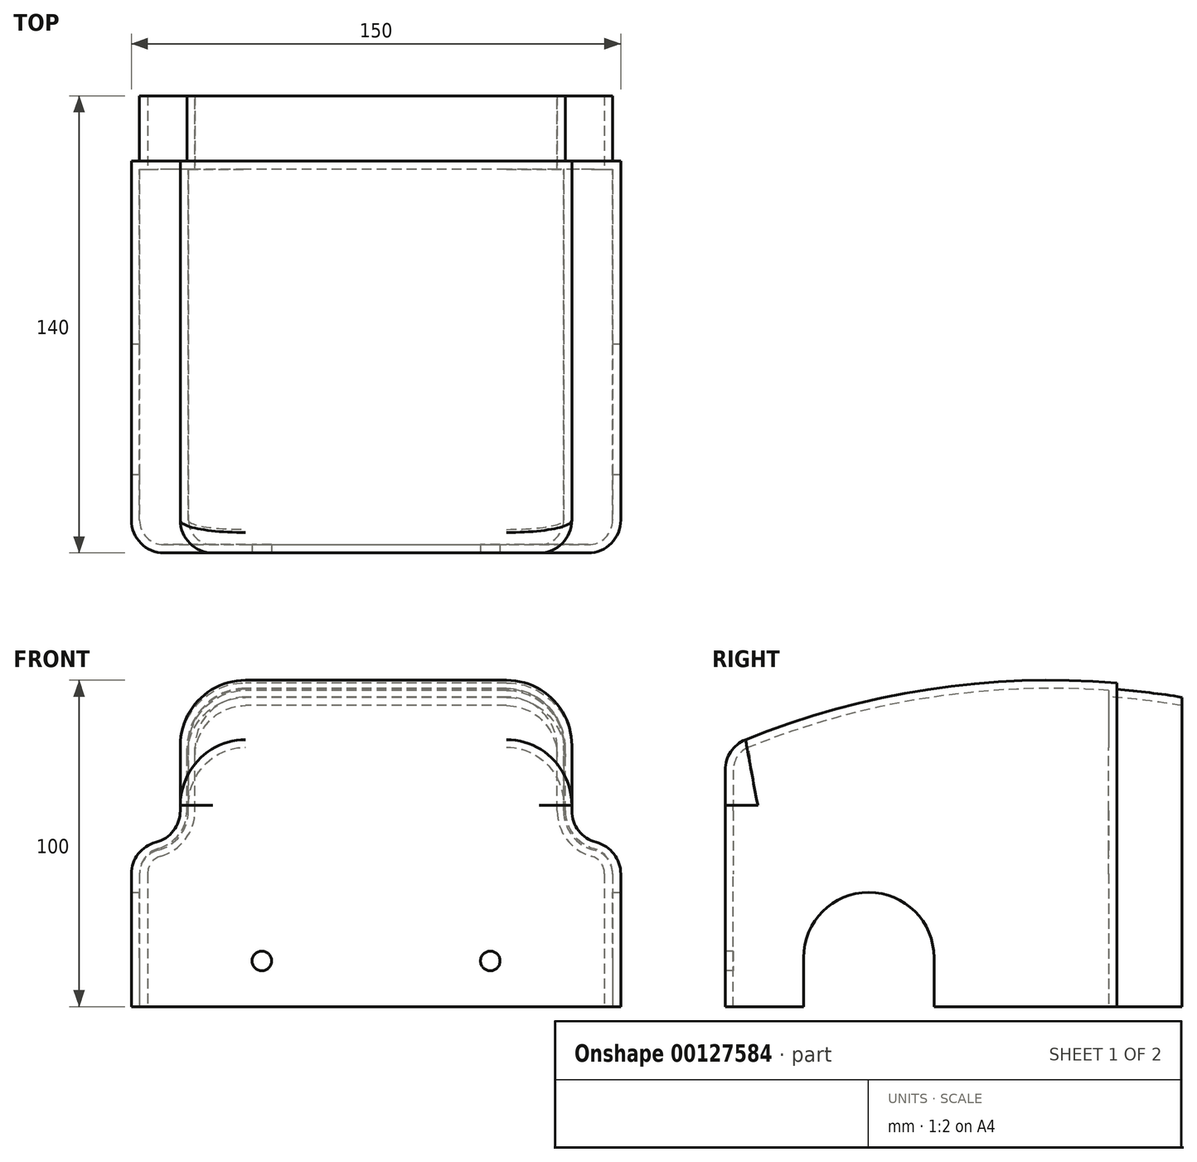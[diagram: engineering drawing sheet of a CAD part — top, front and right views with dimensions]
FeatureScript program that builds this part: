
annotation { "Feature Type Name" : "Feature", "Feature Type Description" : "" }
export const myFeature = defineFeature(function(context is Context, id is Id, definition is map)
    precondition{}
    {
        {
            var Q0;
            Q0=qCreatedBy(makeId("Top.planeOp"),FACE);
            var sketch = newSketch(context, id + "F0", { "sketchPlane" : qUnion([Q0])});
            skLineSegment(sketch, "E0.bottom", {"start": v(-75, 120) * mm, "end": v(75, 120) * mm});
            skLineSegment(sketch, "E0.top", {"start": v(-75, 0) * mm, "end": v(75, 0) * mm});
            skLineSegment(sketch, "E0.left", {"start": v(-75, 120) * mm, "end": v(-75, 0) * mm});
            skLineSegment(sketch, "E0.right", {"start": v(75, 120) * mm, "end": v(75, 0) * mm});
            skSolve(sketch);
        }
        {
            var Q0;
            {var subQ1=sQuery(id+"F0.wireOp",EDGE,"E0.top");Q0=makeQuery(id+"F0.imprint","IMPRINT",FACE,{"disambiguationData":[TD([[makeQuery(id+"F0.imprint","IMPRINT",EDGE,{"derivedFrom":subQ1}),1.0]])]});}
            extrude(context, id + "F1", {"entities" : qUnion([Q0]), "depth" : 50 * mm});
        }
        {
            var Q0;
            Q0=qCreatedBy(makeId("Top.planeOp"),FACE);
            var sketch = newSketch(context, id + "F2", { "sketchPlane" : qUnion([Q0])});
            skLineSegment(sketch, "E1.bottom", {"start": v(72.5, 140) * mm, "end": v(-72.5, 140) * mm});
            skLineSegment(sketch, "E1.top", {"start": v(72.5, 120) * mm, "end": v(-72.5, 120) * mm});
            skLineSegment(sketch, "E1.left", {"start": v(72.5, 140) * mm, "end": v(72.5, 120) * mm});
            skLineSegment(sketch, "E1.right", {"start": v(-72.5, 140) * mm, "end": v(-72.5, 120) * mm});
            skSolve(sketch);
        }
        {
            var Q0;
            Q0=makeQuery(id+"F2.imprint","IMPRINT",FACE,{"disambiguationData":[TD([[makeQuery(id+"F2.imprint","IMPRINT",EDGE,{"derivedFrom":sQuery(id+"F2.wireOp",EDGE,"E1.bottom")}),1.0]])]});
            extrude(context, id + "F3", {"entities" : qUnion([Q0]), "operationType" : NewBodyOperationType.ADD, "depth" : 48 * mm});
        }
        {
            var Q0;
            Q0=qCreatedBy(makeId("Right.planeOp"),FACE);
            var sketch = newSketch(context, id + "F4", { "sketchPlane" : qUnion([Q0])});
            skCircle(sketch, "E2", {"center": v(100, -150) * mm, "radius": 250 * mm});
            skLineSegment(sketch, "E3.bottom", {"start": v(0, 0) * mm, "end": v(120, 0) * mm});
            skLineSegment(sketch, "E3.left", {"start": v(0, 0) * mm, "end": v(0, 79.13) * mm});
            skLineSegment(sketch, "E3.right", {"start": v(120, 0) * mm, "end": v(120, 99.2) * mm});
            skSolve(sketch);
        }
        {
            var Q0;
            {var subQ0=sQuery(id+"F4.wireOp",EDGE,"E3.top");Q0=makeQuery(id+"F4.imprint","IMPRINT",FACE,{"disambiguationData":[TD([[makeQuery(id+"F4.imprint","IMPRINT",EDGE,{"derivedFrom":subQ0}),1.0]])]});}
            var Q1;
            Q1=makeQuery(id+"F4.imprint","IMPRINT",FACE,{"disambiguationData":[TD([[makeQuery(id+"F4.imprint","IMPRINT",EDGE,{"derivedFrom":sQuery(id+"F4.wireOp",EDGE,"E3.bottom")}),1.0]])]});
            extrude(context, id + "F5", {"entities" : qUnion([Q0, Q1]), "operationType" : NewBodyOperationType.ADD, "endBound" : BoundingType.SYMMETRIC, "depth" : 120 * mm});
        }
        {
            var Q0;
            Q0=qCreatedBy(makeId("Right.planeOp"),FACE);
            var sketch = newSketch(context, id + "F6", { "sketchPlane" : qUnion([Q0])});
            skCircle(sketch, "E4", {"center": v(100, -150) * mm, "radius": 248 * mm});
            skLineSegment(sketch, "E5.bottom", {"start": v(0, 0) * mm, "end": v(140, 0) * mm});
            skLineSegment(sketch, "E5.left", {"start": v(0, 0) * mm, "end": v(0, 76.94) * mm});
            skLineSegment(sketch, "E5.right", {"start": v(140, 0) * mm, "end": v(140, 94.75) * mm});
            skLineSegment(sketch, "E6", {"start": v(120, 0) * mm, "end": v(120, 97.2) * mm});
            skSolve(sketch);
        }
        {
            var Q0;
            {var subQ0=sQuery(id+"F6.wireOp",EDGE,"E5.right");Q0=makeQuery(id+"F6.imprint","IMPRINT",FACE,{"disambiguationData":[TD([[makeQuery(id+"F6.imprint","IMPRINT",EDGE,{"derivedFrom":subQ0}),1.0]])]});}
            extrude(context, id + "F7", {"entities" : qUnion([Q0]), "operationType" : NewBodyOperationType.ADD, "endBound" : BoundingType.SYMMETRIC, "depth" : 116 * mm});
        }
        {
            var Q0;
            Q0=makeQuery(id+"F7.opExtrude","CAP_EDGE",EDGE,{"disambiguationData":[OSD([sQuery(id+"F6.wireOp",EDGE,"E4")])],"isStart":false});
            var Q1;
            Q1=makeQuery(id+"F7.opExtrude","CAP_EDGE",EDGE,{"disambiguationData":[OSD([sQuery(id+"F6.wireOp",EDGE,"E4")])],"isStart":true});
            fillet(context, id + "F8", {"entities" : qUnion([Q0, Q1]), "radius" : 18 * mm, "tangentPropagation" : true, "allowEdgeOverflow" : false});
        }
        {
            var Q0;
            Q0=makeQuery(id+"F5.opExtrude","CAP_EDGE",EDGE,{"disambiguationData":[OSD([sQuery(id+"F4.wireOp",EDGE,"E2")])],"isStart":false});
            var Q1;
            Q1=makeQuery(id+"F5.opExtrude","CAP_EDGE",EDGE,{"disambiguationData":[OSD([sQuery(id+"F4.wireOp",EDGE,"E2")])],"isStart":true});
            fillet(context, id + "F9", {"entities" : qUnion([Q0, Q1]), "radius" : 20 * mm, "tangentPropagation" : true, "allowEdgeOverflow" : false});
        }
        {
            var Q0;
            Q0=makeQuery(id+"F5.boolean.opBoolean","INTERSECT",EDGE,{"derivedFrom":[makeQuery(id+"F1.opExtrude","CAP_FACE",FACE,{"disambiguationData":[OSD([sQuery(id+"F0.wireOp",EDGE,"E0.bottom"),sQuery(id+"F0.wireOp",EDGE,"E0.top"),sQuery(id+"F0.wireOp",EDGE,"E0.left"),sQuery(id+"F0.wireOp",EDGE,"E0.right")])],"isStart":false}),makeQuery(id+"F5.opExtrude","CAP_FACE",FACE,{"disambiguationData":[OSD([sQuery(id+"F4.wireOp",EDGE,"E2"),sQuery(id+"F4.wireOp",EDGE,"E3.bottom"),sQuery(id+"F4.wireOp",EDGE,"E3.left"),sQuery(id+"F4.wireOp",EDGE,"E3.right")])],"isStart":true})]});
            var Q1;
            Q1=makeQuery(id+"F5.boolean.opBoolean","INTERSECT",EDGE,{"derivedFrom":[makeQuery(id+"F1.opExtrude","CAP_FACE",FACE,{"disambiguationData":[OSD([sQuery(id+"F0.wireOp",EDGE,"E0.bottom"),sQuery(id+"F0.wireOp",EDGE,"E0.top"),sQuery(id+"F0.wireOp",EDGE,"E0.left"),sQuery(id+"F0.wireOp",EDGE,"E0.right")])],"isStart":false}),makeQuery(id+"F5.opExtrude","CAP_FACE",FACE,{"disambiguationData":[OSD([sQuery(id+"F4.wireOp",EDGE,"E2"),sQuery(id+"F4.wireOp",EDGE,"E3.bottom"),sQuery(id+"F4.wireOp",EDGE,"E3.left"),sQuery(id+"F4.wireOp",EDGE,"E3.right")])],"isStart":false})]});
            fillet(context, id + "F10", {"entities" : qUnion([Q0, Q1]), "radius" : 10 * mm, "tangentPropagation" : true, "allowEdgeOverflow" : false});
        }
        {
            var Q0;
            Q0=makeQuery(id+"F7.boolean.opBoolean","INTERSECT",EDGE,{"derivedFrom":[makeQuery(id+"F3.opExtrude","CAP_FACE",FACE,{"disambiguationData":[OSD([sQuery(id+"F2.wireOp",EDGE,"E1.bottom"),sQuery(id+"F2.wireOp",EDGE,"E1.top"),sQuery(id+"F2.wireOp",EDGE,"E1.left"),sQuery(id+"F2.wireOp",EDGE,"E1.right")])],"isStart":false}),makeQuery(id+"F7.opExtrude","CAP_FACE",FACE,{"disambiguationData":[OSD([sQuery(id+"F6.wireOp",EDGE,"E4"),sQuery(id+"F6.wireOp",EDGE,"E5.bottom"),sQuery(id+"F6.wireOp",EDGE,"E5.right"),sQuery(id+"F6.wireOp",EDGE,"E6")])],"isStart":false})]});
            var Q1;
            Q1=makeQuery(id+"F7.boolean.opBoolean","INTERSECT",EDGE,{"derivedFrom":[makeQuery(id+"F3.opExtrude","CAP_FACE",FACE,{"disambiguationData":[OSD([sQuery(id+"F2.wireOp",EDGE,"E1.bottom"),sQuery(id+"F2.wireOp",EDGE,"E1.top"),sQuery(id+"F2.wireOp",EDGE,"E1.left"),sQuery(id+"F2.wireOp",EDGE,"E1.right")])],"isStart":false}),makeQuery(id+"F7.opExtrude","CAP_FACE",FACE,{"disambiguationData":[OSD([sQuery(id+"F6.wireOp",EDGE,"E4"),sQuery(id+"F6.wireOp",EDGE,"E5.bottom"),sQuery(id+"F6.wireOp",EDGE,"E5.right"),sQuery(id+"F6.wireOp",EDGE,"E6")])],"isStart":true})]});
            fillet(context, id + "F11", {"entities" : qUnion([Q0, Q1]), "radius" : 12 * mm, "tangentPropagation" : true, "allowEdgeOverflow" : false});
        }
        {
            var Q0;
            Q0=makeQuery(id+"F3.opExtrude","CAP_EDGE",EDGE,{"disambiguationData":[OSD([sQuery(id+"F2.wireOp",EDGE,"E1.left")])],"isStart":false});
            var Q1;
            Q1=makeQuery(id+"F3.opExtrude","CAP_EDGE",EDGE,{"disambiguationData":[OSD([sQuery(id+"F2.wireOp",EDGE,"E1.right")])],"isStart":false});
            fillet(context, id + "F12", {"entities" : qUnion([Q0, Q1]), "radius" : 8 * mm, "tangentPropagation" : true, "allowEdgeOverflow" : false});
        }
        {
            var Q0;
            Q0=makeQuery(id+"F1.opExtrude","CAP_EDGE",EDGE,{"disambiguationData":[OSD([sQuery(id+"F0.wireOp",EDGE,"E0.left")])],"isStart":false});
            var Q1;
            Q1=makeQuery(id+"F1.opExtrude","CAP_EDGE",EDGE,{"disambiguationData":[OSD([sQuery(id+"F0.wireOp",EDGE,"E0.right")])],"isStart":false});
            fillet(context, id + "F13", {"entities" : qUnion([Q0, Q1]), "radius" : 10 * mm, "tangentPropagation" : true, "allowEdgeOverflow" : false});
        }
        {
            var Q0;
            Q0=makeQuery(id+"F5.opExtrude","SWEPT_EDGE",EDGE,{"disambiguationData":[OSD([sQuery(id+"F4.wireOp",EDGE,"E2"),sQuery(id+"F4.wireOp",EDGE,"E3.top"),sQuery(id+"F4.wireOp",EDGE,"E3.left")])]});
            fillet(context, id + "F14", {"entities" : qUnion([Q0]), "radius" : 10 * mm, "tangentPropagation" : true, "allowEdgeOverflow" : false});
        }
        {
            var Q0;
            Q0=makeQuery(id+"F1.opExtrude","CAP_FACE",FACE,{"disambiguationData":[OSD([sQuery(id+"F0.wireOp",EDGE,"E0.bottom"),sQuery(id+"F0.wireOp",EDGE,"E0.top"),sQuery(id+"F0.wireOp",EDGE,"E0.left"),sQuery(id+"F0.wireOp",EDGE,"E0.right")])],"isStart":true});
            var Q1;
            Q1=makeQuery(id+"F7.boolean.opBoolean","MERGE",FACE,{"derivedFrom":[makeQuery(id+"F3.opExtrude","SWEPT_FACE",FACE,{"disambiguationData":[OSD([sQuery(id+"F2.wireOp",EDGE,"E1.bottom")])]}),makeQuery(id+"F7.opExtrude","SWEPT_FACE",FACE,{"disambiguationData":[OSD([sQuery(id+"F6.wireOp",EDGE,"E5.right")])]})]});
            shell(context, id + "F15", {"entities" : qUnion([Q0, Q1]), "thickness" : 2.5 * mm});
        }
        {
            var Q0;
            Q0=qCreatedBy(makeId("Right.planeOp"),FACE);
            var sketch = newSketch(context, id + "F16", { "sketchPlane" : qUnion([Q0])});
            skCircle(sketch, "E7", {"center": v(44, 15) * mm, "radius": 20 * mm});
            skLineSegment(sketch, "E8.bottom", {"start": v(24, 15) * mm, "end": v(64, 15) * mm});
            skLineSegment(sketch, "E8.top", {"start": v(24, -35) * mm, "end": v(64, -35) * mm});
            skLineSegment(sketch, "E8.left", {"start": v(24, 15) * mm, "end": v(24, -35) * mm});
            skLineSegment(sketch, "E8.right", {"start": v(64, 15) * mm, "end": v(64, -35) * mm});
            skSolve(sketch);
        }
        {
            var Q0;
            Q0=makeQuery(id+"F16.imprint","IMPRINT",FACE,{"disambiguationData":[TD([[makeQuery(id+"F16.imprint","IMPRINT",EDGE,{"derivedFrom":sQuery(id+"F16.wireOp",EDGE,"E7")}),1.0]])]});
            var Q1;
            Q1=makeQuery(id+"F16.imprint","IMPRINT",FACE,{"disambiguationData":[TD([[makeQuery(id+"F16.imprint","IMPRINT",EDGE,{"derivedFrom":sQuery(id+"F16.wireOp",EDGE,"E8.top")}),1.0]])]});
            extrude(context, id + "F17", {"entities" : qUnion([Q0, Q1]), "operationType" : NewBodyOperationType.REMOVE, "endBound" : BoundingType.SYMMETRIC, "oppositeDirection" : true, "depth" : 200 * mm});
        }
        {
            var Q0;
            Q0=qCreatedBy(makeId("Front.planeOp"),FACE);
            var sketch = newSketch(context, id + "F18", { "sketchPlane" : qUnion([Q0])});
            skCircle(sketch, "E9", {"center": v(-35, 14) * mm, "radius": 3 * mm});
            skCircle(sketch, "E10", {"center": v(35, 14) * mm, "radius": 3 * mm});
            skSolve(sketch);
        }
        {
            var Q0;
            Q0=makeQuery(id+"F18.imprint","IMPRINT",FACE,{"disambiguationData":[TD([[makeQuery(id+"F18.imprint","IMPRINT",EDGE,{"derivedFrom":sQuery(id+"F18.wireOp",EDGE,"E9")}),1.0]])]});
            var Q1;
            Q1=makeQuery(id+"F18.imprint","IMPRINT",FACE,{"disambiguationData":[TD([[makeQuery(id+"F18.imprint","IMPRINT",EDGE,{"derivedFrom":sQuery(id+"F18.wireOp",EDGE,"E10")}),1.0]])]});
            extrude(context, id + "F19", {"entities" : qUnion([Q0, Q1]), "operationType" : NewBodyOperationType.REMOVE, "endBound" : BoundingType.SYMMETRIC, "oppositeDirection" : true, "depth" : 25 * mm});
        }
    });
